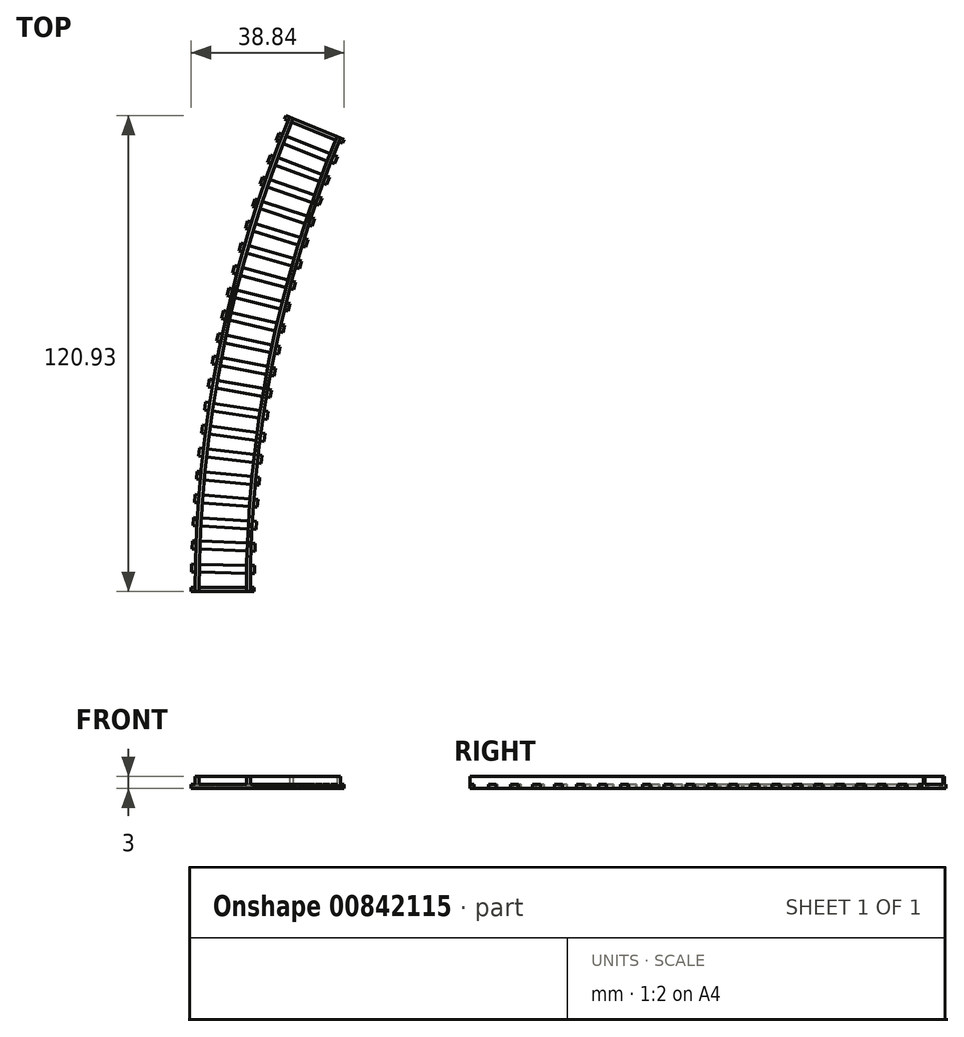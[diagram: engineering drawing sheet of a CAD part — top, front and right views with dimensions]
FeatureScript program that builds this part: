
annotation { "Feature Type Name" : "Feature", "Feature Type Description" : "" }
export const myFeature = defineFeature(function(context is Context, id is Id, definition is map)
    precondition{}
    {
        {
            var Q0;
            Q0=qCreatedBy(makeId("Top.planeOp"),FACE);
            var sketch = newSketch(context, id + "F0", { "sketchPlane" : qUnion([Q0])});
            skCircle(sketch, "E0", {"center": v(0, 0) * mm, "radius": 314 * mm});
            skCircle(sketch, "E1", {"center": v(0, 0) * mm, "radius": 302 * mm});
            skLineSegment(sketch, "E2", {"start": v(0, 0) * mm, "end": v(-293.77, 116.43) * mm});
            skLineSegment(sketch, "E3", {"start": v(0, 0) * mm, "end": v(-369.38, 153) * mm});
            skCircle(sketch, "E4", {"center": v(0, 0) * mm, "radius": 301 * mm});
            skCircle(sketch, "E5", {"center": v(0, 0) * mm, "radius": 315 * mm});
            skLineSegment(sketch, "E6", {"start": v(-293.77, 116.43) * mm, "end": v(-294.5, 114.57) * mm});
            skLineSegment(sketch, "E7", {"start": v(-294.5, 114.57) * mm, "end": v(-279.63, 108.67) * mm});
            skLineSegment(sketch, "E8", {"start": v(-279.63, 108.67) * mm, "end": v(-278.9, 110.53) * mm});
            skLineSegment(sketch, "E9", {"start": v(0, 0) * mm, "end": v(-295.9, 110.91) * mm});
            skLineSegment(sketch, "E10", {"start": v(-295.9, 110.91) * mm, "end": v(-296.6, 109.04) * mm});
            skLineSegment(sketch, "E11", {"start": v(-296.6, 109.04) * mm, "end": v(-281.62, 103.43) * mm});
            skLineSegment(sketch, "E12", {"start": v(-281.62, 103.43) * mm, "end": v(-280.91, 105.3) * mm});
            skLineSegment(sketch, "E13", {"start": v(-280.91, 105.3) * mm, "end": v(-279.63, 108.67) * mm, "construction": true});
            skLineSegment(sketch, "E14", {"start": v(0, 0) * mm, "end": v(-297.92, 105.36) * mm});
            skLineSegment(sketch, "E15", {"start": v(0, 0) * mm, "end": v(-299.84, 99.77) * mm});
            skLineSegment(sketch, "E16", {"start": v(0, 0) * mm, "end": v(-301.65, 94.15) * mm});
            skLineSegment(sketch, "E17", {"start": v(0, 0) * mm, "end": v(-303.36, 88.5) * mm});
            skLineSegment(sketch, "E18", {"start": v(0, 0) * mm, "end": v(-304.96, 82.8) * mm});
            skLineSegment(sketch, "E19", {"start": v(0, 0) * mm, "end": v(-306.45, 77.09) * mm});
            skLineSegment(sketch, "E20", {"start": v(0, 0) * mm, "end": v(-307.84, 71.34) * mm});
            skLineSegment(sketch, "E21", {"start": v(0, 0) * mm, "end": v(-309.12, 65.57) * mm});
            skLineSegment(sketch, "E22", {"start": v(0, 0) * mm, "end": v(-310.3, 59.78) * mm});
            skLineSegment(sketch, "E23", {"start": v(0, 0) * mm, "end": v(-311.36, 53.97) * mm});
            skLineSegment(sketch, "E24", {"start": v(0, 0) * mm, "end": v(-312.31, 48.14) * mm});
            skLineSegment(sketch, "E25", {"start": v(0, 0) * mm, "end": v(-313.16, 42.3) * mm});
            skLineSegment(sketch, "E26", {"start": v(0, 0) * mm, "end": v(-313.9, 36.43) * mm});
            skLineSegment(sketch, "E27", {"start": v(0, 0) * mm, "end": v(-314.52, 30.55) * mm});
            skLineSegment(sketch, "E28", {"start": v(0, 0) * mm, "end": v(-315.04, 24.66) * mm});
            skLineSegment(sketch, "E29", {"start": v(0, 0) * mm, "end": v(-315.44, 18.77) * mm});
            skLineSegment(sketch, "E30", {"start": v(-297.92, 105.36) * mm, "end": v(-298.58, 103.48) * mm});
            skLineSegment(sketch, "E31", {"start": v(-298.58, 103.48) * mm, "end": v(-283.5, 98.14) * mm});
            skLineSegment(sketch, "E32", {"start": v(-283.5, 98.14) * mm, "end": v(-282.83, 100.03) * mm});
            skLineSegment(sketch, "E33", {"start": v(-299.84, 99.77) * mm, "end": v(-300.47, 97.87) * mm});
            skLineSegment(sketch, "E34", {"start": v(-300.47, 97.87) * mm, "end": v(-285.29, 92.82) * mm});
            skLineSegment(sketch, "E35", {"start": v(-285.29, 92.82) * mm, "end": v(-284.65, 94.72) * mm});
            skLineSegment(sketch, "E36", {"start": v(-301.65, 94.15) * mm, "end": v(-302.24, 92.24) * mm});
            skLineSegment(sketch, "E37", {"start": v(-302.24, 92.24) * mm, "end": v(-286.97, 87.47) * mm});
            skLineSegment(sketch, "E38", {"start": v(-286.97, 87.47) * mm, "end": v(-286.38, 89.38) * mm});
            skLineSegment(sketch, "E39", {"start": v(-303.36, 88.5) * mm, "end": v(-303.92, 86.57) * mm});
            skLineSegment(sketch, "E40", {"start": v(-303.92, 86.57) * mm, "end": v(-288.56, 82.1) * mm});
            skLineSegment(sketch, "E41", {"start": v(-288.56, 82.1) * mm, "end": v(-288, 84.01) * mm});
            skLineSegment(sketch, "E42", {"start": v(-304.96, 82.8) * mm, "end": v(-305.48, 80.87) * mm});
            skLineSegment(sketch, "E43", {"start": v(-305.48, 80.87) * mm, "end": v(-290.04, 76.68) * mm});
            skLineSegment(sketch, "E44", {"start": v(-290.04, 76.68) * mm, "end": v(-289.52, 78.61) * mm});
            skLineSegment(sketch, "E45", {"start": v(-306.45, 77.09) * mm, "end": v(-306.94, 75.15) * mm});
            skLineSegment(sketch, "E46", {"start": v(-306.94, 75.15) * mm, "end": v(-291.42, 71.24) * mm});
            skLineSegment(sketch, "E47", {"start": v(-291.42, 71.24) * mm, "end": v(-290.94, 73.18) * mm});
            skLineSegment(sketch, "E48", {"start": v(-307.84, 71.34) * mm, "end": v(-308.3, 69.4) * mm});
            skLineSegment(sketch, "E49", {"start": v(-308.3, 69.4) * mm, "end": v(-292.7, 65.78) * mm});
            skLineSegment(sketch, "E50", {"start": v(-292.7, 65.78) * mm, "end": v(-292.25, 67.73) * mm});
            skLineSegment(sketch, "E51", {"start": v(-309.12, 65.57) * mm, "end": v(-309.54, 63.62) * mm});
            skLineSegment(sketch, "E52", {"start": v(-309.54, 63.62) * mm, "end": v(-293.88, 60.3) * mm});
            skLineSegment(sketch, "E53", {"start": v(-293.88, 60.3) * mm, "end": v(-293.47, 62.25) * mm});
            skLineSegment(sketch, "E54", {"start": v(-310.3, 59.78) * mm, "end": v(-310.67, 57.82) * mm});
            skLineSegment(sketch, "E55", {"start": v(-310.67, 57.82) * mm, "end": v(-294.96, 54.8) * mm});
            skLineSegment(sketch, "E56", {"start": v(-294.96, 54.8) * mm, "end": v(-294.58, 56.76) * mm});
            skLineSegment(sketch, "E57", {"start": v(-311.36, 53.97) * mm, "end": v(-311.7, 52) * mm});
            skLineSegment(sketch, "E58", {"start": v(-311.7, 52) * mm, "end": v(-295.93, 49.27) * mm});
            skLineSegment(sketch, "E59", {"start": v(-295.93, 49.27) * mm, "end": v(-295.6, 51.24) * mm});
            skLineSegment(sketch, "E60", {"start": v(-312.31, 48.14) * mm, "end": v(-312.62, 46.16) * mm});
            skLineSegment(sketch, "E61", {"start": v(-312.62, 46.16) * mm, "end": v(-296.8, 43.72) * mm});
            skLineSegment(sketch, "E62", {"start": v(-296.8, 43.72) * mm, "end": v(-296.5, 45.7) * mm});
            skLineSegment(sketch, "E63", {"start": v(-313.16, 42.3) * mm, "end": v(-313.43, 40.3) * mm});
            skLineSegment(sketch, "E64", {"start": v(-313.43, 40.3) * mm, "end": v(-297.57, 38.17) * mm});
            skLineSegment(sketch, "E65", {"start": v(-297.57, 38.17) * mm, "end": v(-297.3, 40.15) * mm});
            skLineSegment(sketch, "E66", {"start": v(-313.9, 36.43) * mm, "end": v(-314.12, 34.44) * mm});
            skLineSegment(sketch, "E67", {"start": v(-314.12, 34.44) * mm, "end": v(-298.23, 32.6) * mm});
            skLineSegment(sketch, "E68", {"start": v(-298.23, 32.6) * mm, "end": v(-298, 34.58) * mm});
            skLineSegment(sketch, "E69", {"start": v(-314.52, 30.55) * mm, "end": v(-314.71, 28.56) * mm});
            skLineSegment(sketch, "E70", {"start": v(-314.71, 28.56) * mm, "end": v(-298.79, 27.01) * mm});
            skLineSegment(sketch, "E71", {"start": v(-298.79, 27.01) * mm, "end": v(-298.6, 29) * mm});
            skLineSegment(sketch, "E72", {"start": v(-315.04, 24.66) * mm, "end": v(-315.2, 22.67) * mm});
            skLineSegment(sketch, "E73", {"start": v(-315.2, 22.67) * mm, "end": v(-299.24, 21.42) * mm});
            skLineSegment(sketch, "E74", {"start": v(-299.24, 21.42) * mm, "end": v(-299.08, 23.42) * mm});
            skLineSegment(sketch, "E75", {"start": v(-315.44, 18.77) * mm, "end": v(-315.56, 16.77) * mm});
            skLineSegment(sketch, "E76", {"start": v(-315.56, 16.77) * mm, "end": v(-299.59, 15.82) * mm});
            skLineSegment(sketch, "E77", {"start": v(-299.59, 15.82) * mm, "end": v(-299.47, 17.82) * mm});
            skLineSegment(sketch, "E78", {"start": v(-281.62, 103.43) * mm, "end": v(-282.83, 100.03) * mm, "construction": true});
            skLineSegment(sketch, "E79", {"start": v(-283.5, 98.14) * mm, "end": v(-284.65, 94.72) * mm, "construction": true});
            skLineSegment(sketch, "E80", {"start": v(-285.29, 92.82) * mm, "end": v(-286.38, 89.38) * mm, "construction": true});
            skLineSegment(sketch, "E81", {"start": v(-286.97, 87.47) * mm, "end": v(-288, 84.01) * mm, "construction": true});
            skLineSegment(sketch, "E82", {"start": v(-288.56, 82.1) * mm, "end": v(-289.52, 78.61) * mm, "construction": true});
            skLineSegment(sketch, "E83", {"start": v(-290.04, 76.68) * mm, "end": v(-290.94, 73.18) * mm, "construction": true});
            skLineSegment(sketch, "E84", {"start": v(-291.42, 71.24) * mm, "end": v(-292.25, 67.73) * mm, "construction": true});
            skLineSegment(sketch, "E85", {"start": v(-292.7, 65.78) * mm, "end": v(-293.47, 62.25) * mm, "construction": true});
            skLineSegment(sketch, "E86", {"start": v(-293.88, 60.3) * mm, "end": v(-294.58, 56.76) * mm, "construction": true});
            skLineSegment(sketch, "E87", {"start": v(-294.96, 54.8) * mm, "end": v(-295.6, 51.24) * mm, "construction": true});
            skLineSegment(sketch, "E88", {"start": v(-295.93, 49.27) * mm, "end": v(-296.5, 45.7) * mm, "construction": true});
            skLineSegment(sketch, "E89", {"start": v(-296.8, 43.72) * mm, "end": v(-297.3, 40.15) * mm, "construction": true});
            skLineSegment(sketch, "E90", {"start": v(-297.57, 38.17) * mm, "end": v(-298, 34.58) * mm, "construction": true});
            skLineSegment(sketch, "E91", {"start": v(-298.23, 32.6) * mm, "end": v(-298.6, 29) * mm, "construction": true});
            skLineSegment(sketch, "E92", {"start": v(-298.79, 27.01) * mm, "end": v(-299.08, 23.42) * mm, "construction": true});
            skLineSegment(sketch, "E93", {"start": v(-299.24, 21.42) * mm, "end": v(-299.47, 17.82) * mm, "construction": true});
            skLineSegment(sketch, "E94", {"start": v(0, 0) * mm, "end": v(-315.74, 12.87) * mm});
            skLineSegment(sketch, "E95", {"start": v(-315.74, 12.87) * mm, "end": v(-315.82, 10.87) * mm});
            skLineSegment(sketch, "E96", {"start": v(-315.82, 10.87) * mm, "end": v(-299.83, 10.22) * mm});
            skLineSegment(sketch, "E97", {"start": v(-299.83, 10.22) * mm, "end": v(-299.75, 12.22) * mm});
            skLineSegment(sketch, "E98", {"start": v(-299.75, 12.22) * mm, "end": v(-299.59, 15.82) * mm, "construction": true});
            skLineSegment(sketch, "E99.bottom", {"start": v(-469.53, 106.99) * mm, "end": v(-349.53, 106.99) * mm, "construction": true});
            skLineSegment(sketch, "E99.top", {"start": v(-469.53, -13.01) * mm, "end": v(-349.53, -13.01) * mm, "construction": true});
            skLineSegment(sketch, "E99.left", {"start": v(-469.53, 106.99) * mm, "end": v(-469.53, -13.01) * mm, "construction": true});
            skLineSegment(sketch, "E99.right", {"start": v(-349.53, 106.99) * mm, "end": v(-349.53, -13.01) * mm, "construction": true});
            skLineSegment(sketch, "E100", {"start": v(-301, 0) * mm, "end": v(-315, 0) * mm});
            skLineSegment(sketch, "E101", {"start": v(0, 0) * mm, "end": v(-291.95, 120.93) * mm});
            skLineSegment(sketch, "E102", {"start": v(-291.95, 120.93) * mm, "end": v(-292.33, 120) * mm});
            skLineSegment(sketch, "E103", {"start": v(-292.33, 120) * mm, "end": v(-277.55, 113.88) * mm});
            skLineSegment(sketch, "E104", {"start": v(-277.55, 113.88) * mm, "end": v(-277.16, 114.8) * mm});
            skLineSegment(sketch, "E105", {"start": v(-277.16, 114.8) * mm, "end": v(-277.16, 114.8) * mm});
            skLineSegment(sketch, "E106", {"start": v(-278.9, 110.53) * mm, "end": v(-277.55, 113.88) * mm, "construction": true});
            skLineSegment(sketch, "E107", {"start": v(0, 0) * mm, "end": v(-315.92, 6.96) * mm});
            skLineSegment(sketch, "E108", {"start": v(0, 0) * mm, "end": v(-316, 0) * mm});
            skLineSegment(sketch, "E109", {"start": v(-316, 1) * mm, "end": v(-316, 0) * mm});
            skLineSegment(sketch, "E110", {"start": v(-316, 1) * mm, "end": v(-300, 1) * mm});
            skLineSegment(sketch, "E111", {"start": v(-300, 0) * mm, "end": v(-300, 1) * mm});
            skLineSegment(sketch, "E112", {"start": v(-315.92, 6.96) * mm, "end": v(-315.97, 4.96) * mm});
            skLineSegment(sketch, "E113", {"start": v(-315.97, 4.96) * mm, "end": v(-299.97, 4.6) * mm});
            skLineSegment(sketch, "E114", {"start": v(-299.97, 4.6) * mm, "end": v(-299.97, 6.61) * mm});
            skLineSegment(sketch, "E115", {"start": v(-299.97, 6.61) * mm, "end": v(-299.83, 10.22) * mm, "construction": true});
            skLineSegment(sketch, "E116", {"start": v(-299.97, 4.6) * mm, "end": v(-300, 1) * mm, "construction": true});
            skSolve(sketch);
        }
        {
            var Q0;
            {var subQ0=sQuery(id+"F0.wireOp",EDGE,"E103");var subQ1=sQuery(id+"F0.wireOp",EDGE,"E0");var subQ2=makeQuery(id+"F0.imprint","INTERSECT",VERTEX,{"derivedFrom":[subQ1,subQ0]});Q0=makeQuery(id+"F0.imprint","IMPRINT",FACE,{"disambiguationData":[TD([[makeQuery(id+"F0.imprint","IMPRINT",EDGE,{"disambiguationData":[TD([[subQ2,-1.0]])],"derivedFrom":subQ1}),-1.0]])]});}
            var Q1;
            {var subQ0=sQuery(id+"F0.wireOp",EDGE,"E7");var subQ1=sQuery(id+"F0.wireOp",EDGE,"E0");var subQ2=makeQuery(id+"F0.imprint","INTERSECT",VERTEX,{"derivedFrom":[subQ1,subQ0]});Q1=makeQuery(id+"F0.imprint","IMPRINT",FACE,{"disambiguationData":[TD([[makeQuery(id+"F0.imprint","IMPRINT",EDGE,{"disambiguationData":[TD([[subQ2,-1.0]])],"derivedFrom":subQ1}),-1.0]])]});}
            var Q2;
            {var subQ0=sQuery(id+"F0.wireOp",EDGE,"E11");var subQ1=sQuery(id+"F0.wireOp",EDGE,"E0");var subQ2=makeQuery(id+"F0.imprint","INTERSECT",VERTEX,{"derivedFrom":[subQ1,subQ0]});Q2=makeQuery(id+"F0.imprint","IMPRINT",FACE,{"disambiguationData":[TD([[makeQuery(id+"F0.imprint","IMPRINT",EDGE,{"disambiguationData":[TD([[subQ2,-1.0]])],"derivedFrom":subQ1}),-1.0]])]});}
            var Q3;
            {var subQ0=sQuery(id+"F0.wireOp",EDGE,"E31");var subQ1=sQuery(id+"F0.wireOp",EDGE,"E0");var subQ2=makeQuery(id+"F0.imprint","INTERSECT",VERTEX,{"derivedFrom":[subQ1,subQ0]});Q3=makeQuery(id+"F0.imprint","IMPRINT",FACE,{"disambiguationData":[TD([[makeQuery(id+"F0.imprint","IMPRINT",EDGE,{"disambiguationData":[TD([[subQ2,-1.0]])],"derivedFrom":subQ1}),-1.0]])]});}
            var Q4;
            {var subQ0=sQuery(id+"F0.wireOp",EDGE,"E34");var subQ1=sQuery(id+"F0.wireOp",EDGE,"E0");var subQ2=makeQuery(id+"F0.imprint","INTERSECT",VERTEX,{"derivedFrom":[subQ1,subQ0]});Q4=makeQuery(id+"F0.imprint","IMPRINT",FACE,{"disambiguationData":[TD([[makeQuery(id+"F0.imprint","IMPRINT",EDGE,{"disambiguationData":[TD([[subQ2,-1.0]])],"derivedFrom":subQ1}),-1.0]])]});}
            var Q5;
            {var subQ0=sQuery(id+"F0.wireOp",EDGE,"E37");var subQ1=sQuery(id+"F0.wireOp",EDGE,"E0");var subQ2=makeQuery(id+"F0.imprint","INTERSECT",VERTEX,{"derivedFrom":[subQ1,subQ0]});Q5=makeQuery(id+"F0.imprint","IMPRINT",FACE,{"disambiguationData":[TD([[makeQuery(id+"F0.imprint","IMPRINT",EDGE,{"disambiguationData":[TD([[subQ2,-1.0]])],"derivedFrom":subQ1}),-1.0]])]});}
            var Q6;
            {var subQ0=sQuery(id+"F0.wireOp",EDGE,"E40");var subQ1=sQuery(id+"F0.wireOp",EDGE,"E0");var subQ2=makeQuery(id+"F0.imprint","INTERSECT",VERTEX,{"derivedFrom":[subQ1,subQ0]});Q6=makeQuery(id+"F0.imprint","IMPRINT",FACE,{"disambiguationData":[TD([[makeQuery(id+"F0.imprint","IMPRINT",EDGE,{"disambiguationData":[TD([[subQ2,-1.0]])],"derivedFrom":subQ1}),-1.0]])]});}
            var Q7;
            {var subQ0=sQuery(id+"F0.wireOp",EDGE,"E43");var subQ1=sQuery(id+"F0.wireOp",EDGE,"E0");var subQ2=makeQuery(id+"F0.imprint","INTERSECT",VERTEX,{"derivedFrom":[subQ1,subQ0]});Q7=makeQuery(id+"F0.imprint","IMPRINT",FACE,{"disambiguationData":[TD([[makeQuery(id+"F0.imprint","IMPRINT",EDGE,{"disambiguationData":[TD([[subQ2,-1.0]])],"derivedFrom":subQ1}),-1.0]])]});}
            var Q8;
            {var subQ0=sQuery(id+"F0.wireOp",EDGE,"E46");var subQ1=sQuery(id+"F0.wireOp",EDGE,"E0");var subQ2=makeQuery(id+"F0.imprint","INTERSECT",VERTEX,{"derivedFrom":[subQ1,subQ0]});Q8=makeQuery(id+"F0.imprint","IMPRINT",FACE,{"disambiguationData":[TD([[makeQuery(id+"F0.imprint","IMPRINT",EDGE,{"disambiguationData":[TD([[subQ2,-1.0]])],"derivedFrom":subQ1}),-1.0]])]});}
            var Q9;
            {var subQ0=sQuery(id+"F0.wireOp",EDGE,"E49");var subQ1=sQuery(id+"F0.wireOp",EDGE,"E0");var subQ2=makeQuery(id+"F0.imprint","INTERSECT",VERTEX,{"derivedFrom":[subQ1,subQ0]});Q9=makeQuery(id+"F0.imprint","IMPRINT",FACE,{"disambiguationData":[TD([[makeQuery(id+"F0.imprint","IMPRINT",EDGE,{"disambiguationData":[TD([[subQ2,-1.0]])],"derivedFrom":subQ1}),-1.0]])]});}
            var Q10;
            {var subQ0=sQuery(id+"F0.wireOp",EDGE,"E52");var subQ1=sQuery(id+"F0.wireOp",EDGE,"E0");var subQ2=makeQuery(id+"F0.imprint","INTERSECT",VERTEX,{"derivedFrom":[subQ1,subQ0]});Q10=makeQuery(id+"F0.imprint","IMPRINT",FACE,{"disambiguationData":[TD([[makeQuery(id+"F0.imprint","IMPRINT",EDGE,{"disambiguationData":[TD([[subQ2,-1.0]])],"derivedFrom":subQ1}),-1.0]])]});}
            var Q11;
            {var subQ0=sQuery(id+"F0.wireOp",EDGE,"E55");var subQ1=sQuery(id+"F0.wireOp",EDGE,"E0");var subQ2=makeQuery(id+"F0.imprint","INTERSECT",VERTEX,{"derivedFrom":[subQ1,subQ0]});Q11=makeQuery(id+"F0.imprint","IMPRINT",FACE,{"disambiguationData":[TD([[makeQuery(id+"F0.imprint","IMPRINT",EDGE,{"disambiguationData":[TD([[subQ2,-1.0]])],"derivedFrom":subQ1}),-1.0]])]});}
            var Q12;
            {var subQ0=sQuery(id+"F0.wireOp",EDGE,"E58");var subQ1=sQuery(id+"F0.wireOp",EDGE,"E0");var subQ2=makeQuery(id+"F0.imprint","INTERSECT",VERTEX,{"derivedFrom":[subQ1,subQ0]});Q12=makeQuery(id+"F0.imprint","IMPRINT",FACE,{"disambiguationData":[TD([[makeQuery(id+"F0.imprint","IMPRINT",EDGE,{"disambiguationData":[TD([[subQ2,-1.0]])],"derivedFrom":subQ1}),-1.0]])]});}
            var Q13;
            {var subQ0=sQuery(id+"F0.wireOp",EDGE,"E61");var subQ1=sQuery(id+"F0.wireOp",EDGE,"E0");var subQ2=makeQuery(id+"F0.imprint","INTERSECT",VERTEX,{"derivedFrom":[subQ1,subQ0]});Q13=makeQuery(id+"F0.imprint","IMPRINT",FACE,{"disambiguationData":[TD([[makeQuery(id+"F0.imprint","IMPRINT",EDGE,{"disambiguationData":[TD([[subQ2,-1.0]])],"derivedFrom":subQ1}),-1.0]])]});}
            var Q14;
            {var subQ0=sQuery(id+"F0.wireOp",EDGE,"E64");var subQ1=sQuery(id+"F0.wireOp",EDGE,"E0");var subQ2=makeQuery(id+"F0.imprint","INTERSECT",VERTEX,{"derivedFrom":[subQ1,subQ0]});Q14=makeQuery(id+"F0.imprint","IMPRINT",FACE,{"disambiguationData":[TD([[makeQuery(id+"F0.imprint","IMPRINT",EDGE,{"disambiguationData":[TD([[subQ2,-1.0]])],"derivedFrom":subQ1}),-1.0]])]});}
            var Q15;
            {var subQ0=sQuery(id+"F0.wireOp",EDGE,"E67");var subQ1=sQuery(id+"F0.wireOp",EDGE,"E0");var subQ2=makeQuery(id+"F0.imprint","INTERSECT",VERTEX,{"derivedFrom":[subQ1,subQ0]});Q15=makeQuery(id+"F0.imprint","IMPRINT",FACE,{"disambiguationData":[TD([[makeQuery(id+"F0.imprint","IMPRINT",EDGE,{"disambiguationData":[TD([[subQ2,-1.0]])],"derivedFrom":subQ1}),-1.0]])]});}
            var Q16;
            {var subQ0=sQuery(id+"F0.wireOp",EDGE,"E70");var subQ1=sQuery(id+"F0.wireOp",EDGE,"E0");var subQ2=makeQuery(id+"F0.imprint","INTERSECT",VERTEX,{"derivedFrom":[subQ1,subQ0]});Q16=makeQuery(id+"F0.imprint","IMPRINT",FACE,{"disambiguationData":[TD([[makeQuery(id+"F0.imprint","IMPRINT",EDGE,{"disambiguationData":[TD([[subQ2,-1.0]])],"derivedFrom":subQ1}),-1.0]])]});}
            var Q17;
            {var subQ0=sQuery(id+"F0.wireOp",EDGE,"E73");var subQ1=sQuery(id+"F0.wireOp",EDGE,"E0");var subQ2=makeQuery(id+"F0.imprint","INTERSECT",VERTEX,{"derivedFrom":[subQ1,subQ0]});Q17=makeQuery(id+"F0.imprint","IMPRINT",FACE,{"disambiguationData":[TD([[makeQuery(id+"F0.imprint","IMPRINT",EDGE,{"disambiguationData":[TD([[subQ2,-1.0]])],"derivedFrom":subQ1}),-1.0]])]});}
            var Q18;
            {var subQ0=sQuery(id+"F0.wireOp",EDGE,"E76");var subQ1=sQuery(id+"F0.wireOp",EDGE,"E0");var subQ2=makeQuery(id+"F0.imprint","INTERSECT",VERTEX,{"derivedFrom":[subQ1,subQ0]});Q18=makeQuery(id+"F0.imprint","IMPRINT",FACE,{"disambiguationData":[TD([[makeQuery(id+"F0.imprint","IMPRINT",EDGE,{"disambiguationData":[TD([[subQ2,-1.0]])],"derivedFrom":subQ1}),-1.0]])]});}
            var Q19;
            {var subQ0=sQuery(id+"F0.wireOp",EDGE,"E96");var subQ1=sQuery(id+"F0.wireOp",EDGE,"E0");var subQ2=makeQuery(id+"F0.imprint","INTERSECT",VERTEX,{"derivedFrom":[subQ1,subQ0]});Q19=makeQuery(id+"F0.imprint","IMPRINT",FACE,{"disambiguationData":[TD([[makeQuery(id+"F0.imprint","IMPRINT",EDGE,{"disambiguationData":[TD([[subQ2,-1.0]])],"derivedFrom":subQ1}),-1.0]])]});}
            var Q20;
            {var subQ0=sQuery(id+"F0.wireOp",EDGE,"E113");var subQ1=sQuery(id+"F0.wireOp",EDGE,"E0");var subQ2=makeQuery(id+"F0.imprint","INTERSECT",VERTEX,{"derivedFrom":[subQ1,subQ0]});Q20=makeQuery(id+"F0.imprint","IMPRINT",FACE,{"disambiguationData":[TD([[makeQuery(id+"F0.imprint","IMPRINT",EDGE,{"disambiguationData":[TD([[subQ2,-1.0]])],"derivedFrom":subQ1}),-1.0]])]});}
            var Q21;
            {var subQ0=sQuery(id+"F0.wireOp",EDGE,"E103");var subQ1=sQuery(id+"F0.wireOp",EDGE,"E0");var subQ2=makeQuery(id+"F0.imprint","INTERSECT",VERTEX,{"derivedFrom":[subQ1,subQ0]});Q21=makeQuery(id+"F0.imprint","IMPRINT",FACE,{"disambiguationData":[TD([[makeQuery(id+"F0.imprint","IMPRINT",EDGE,{"disambiguationData":[TD([[subQ2,1.0]])],"derivedFrom":subQ1}),-1.0]])]});}
            var Q22;
            {var subQ0=sQuery(id+"F0.wireOp",EDGE,"E2");var subQ1=sQuery(id+"F0.wireOp",EDGE,"E0");var subQ2=makeQuery(id+"F0.imprint","INTERSECT",VERTEX,{"derivedFrom":[subQ1,subQ0]});Q22=makeQuery(id+"F0.imprint","IMPRINT",FACE,{"disambiguationData":[TD([[makeQuery(id+"F0.imprint","IMPRINT",EDGE,{"disambiguationData":[TD([[subQ2,-1.0]])],"derivedFrom":subQ1}),-1.0]])]});}
            var Q23;
            {var subQ0=sQuery(id+"F0.wireOp",EDGE,"E9");var subQ1=sQuery(id+"F0.wireOp",EDGE,"E0");var subQ2=makeQuery(id+"F0.imprint","INTERSECT",VERTEX,{"derivedFrom":[subQ1,subQ0]});Q23=makeQuery(id+"F0.imprint","IMPRINT",FACE,{"disambiguationData":[TD([[makeQuery(id+"F0.imprint","IMPRINT",EDGE,{"disambiguationData":[TD([[subQ2,-1.0]])],"derivedFrom":subQ1}),-1.0]])]});}
            var Q24;
            {var subQ0=sQuery(id+"F0.wireOp",EDGE,"E14");var subQ1=sQuery(id+"F0.wireOp",EDGE,"E0");var subQ2=makeQuery(id+"F0.imprint","INTERSECT",VERTEX,{"derivedFrom":[subQ1,subQ0]});Q24=makeQuery(id+"F0.imprint","IMPRINT",FACE,{"disambiguationData":[TD([[makeQuery(id+"F0.imprint","IMPRINT",EDGE,{"disambiguationData":[TD([[subQ2,-1.0]])],"derivedFrom":subQ1}),-1.0]])]});}
            var Q25;
            {var subQ0=sQuery(id+"F0.wireOp",EDGE,"E15");var subQ1=sQuery(id+"F0.wireOp",EDGE,"E0");var subQ2=makeQuery(id+"F0.imprint","INTERSECT",VERTEX,{"derivedFrom":[subQ1,subQ0]});Q25=makeQuery(id+"F0.imprint","IMPRINT",FACE,{"disambiguationData":[TD([[makeQuery(id+"F0.imprint","IMPRINT",EDGE,{"disambiguationData":[TD([[subQ2,-1.0]])],"derivedFrom":subQ1}),-1.0]])]});}
            var Q26;
            {var subQ0=sQuery(id+"F0.wireOp",EDGE,"E16");var subQ1=sQuery(id+"F0.wireOp",EDGE,"E0");var subQ2=makeQuery(id+"F0.imprint","INTERSECT",VERTEX,{"derivedFrom":[subQ1,subQ0]});Q26=makeQuery(id+"F0.imprint","IMPRINT",FACE,{"disambiguationData":[TD([[makeQuery(id+"F0.imprint","IMPRINT",EDGE,{"disambiguationData":[TD([[subQ2,-1.0]])],"derivedFrom":subQ1}),-1.0]])]});}
            var Q27;
            {var subQ0=sQuery(id+"F0.wireOp",EDGE,"E17");var subQ1=sQuery(id+"F0.wireOp",EDGE,"E0");var subQ2=makeQuery(id+"F0.imprint","INTERSECT",VERTEX,{"derivedFrom":[subQ1,subQ0]});Q27=makeQuery(id+"F0.imprint","IMPRINT",FACE,{"disambiguationData":[TD([[makeQuery(id+"F0.imprint","IMPRINT",EDGE,{"disambiguationData":[TD([[subQ2,-1.0]])],"derivedFrom":subQ1}),-1.0]])]});}
            var Q28;
            {var subQ0=sQuery(id+"F0.wireOp",EDGE,"E18");var subQ1=sQuery(id+"F0.wireOp",EDGE,"E0");var subQ2=makeQuery(id+"F0.imprint","INTERSECT",VERTEX,{"derivedFrom":[subQ1,subQ0]});Q28=makeQuery(id+"F0.imprint","IMPRINT",FACE,{"disambiguationData":[TD([[makeQuery(id+"F0.imprint","IMPRINT",EDGE,{"disambiguationData":[TD([[subQ2,-1.0]])],"derivedFrom":subQ1}),-1.0]])]});}
            var Q29;
            {var subQ0=sQuery(id+"F0.wireOp",EDGE,"E19");var subQ1=sQuery(id+"F0.wireOp",EDGE,"E0");var subQ2=makeQuery(id+"F0.imprint","INTERSECT",VERTEX,{"derivedFrom":[subQ1,subQ0]});Q29=makeQuery(id+"F0.imprint","IMPRINT",FACE,{"disambiguationData":[TD([[makeQuery(id+"F0.imprint","IMPRINT",EDGE,{"disambiguationData":[TD([[subQ2,-1.0]])],"derivedFrom":subQ1}),-1.0]])]});}
            var Q30;
            {var subQ0=sQuery(id+"F0.wireOp",EDGE,"E20");var subQ1=sQuery(id+"F0.wireOp",EDGE,"E0");var subQ2=makeQuery(id+"F0.imprint","INTERSECT",VERTEX,{"derivedFrom":[subQ1,subQ0]});Q30=makeQuery(id+"F0.imprint","IMPRINT",FACE,{"disambiguationData":[TD([[makeQuery(id+"F0.imprint","IMPRINT",EDGE,{"disambiguationData":[TD([[subQ2,-1.0]])],"derivedFrom":subQ1}),-1.0]])]});}
            var Q31;
            {var subQ0=sQuery(id+"F0.wireOp",EDGE,"E21");var subQ1=sQuery(id+"F0.wireOp",EDGE,"E0");var subQ2=makeQuery(id+"F0.imprint","INTERSECT",VERTEX,{"derivedFrom":[subQ1,subQ0]});Q31=makeQuery(id+"F0.imprint","IMPRINT",FACE,{"disambiguationData":[TD([[makeQuery(id+"F0.imprint","IMPRINT",EDGE,{"disambiguationData":[TD([[subQ2,-1.0]])],"derivedFrom":subQ1}),-1.0]])]});}
            var Q32;
            {var subQ0=sQuery(id+"F0.wireOp",EDGE,"E22");var subQ1=sQuery(id+"F0.wireOp",EDGE,"E0");var subQ2=makeQuery(id+"F0.imprint","INTERSECT",VERTEX,{"derivedFrom":[subQ1,subQ0]});Q32=makeQuery(id+"F0.imprint","IMPRINT",FACE,{"disambiguationData":[TD([[makeQuery(id+"F0.imprint","IMPRINT",EDGE,{"disambiguationData":[TD([[subQ2,-1.0]])],"derivedFrom":subQ1}),-1.0]])]});}
            var Q33;
            {var subQ0=sQuery(id+"F0.wireOp",EDGE,"E23");var subQ1=sQuery(id+"F0.wireOp",EDGE,"E0");var subQ2=makeQuery(id+"F0.imprint","INTERSECT",VERTEX,{"derivedFrom":[subQ1,subQ0]});Q33=makeQuery(id+"F0.imprint","IMPRINT",FACE,{"disambiguationData":[TD([[makeQuery(id+"F0.imprint","IMPRINT",EDGE,{"disambiguationData":[TD([[subQ2,-1.0]])],"derivedFrom":subQ1}),-1.0]])]});}
            var Q34;
            {var subQ0=sQuery(id+"F0.wireOp",EDGE,"E24");var subQ1=sQuery(id+"F0.wireOp",EDGE,"E0");var subQ2=makeQuery(id+"F0.imprint","INTERSECT",VERTEX,{"derivedFrom":[subQ1,subQ0]});Q34=makeQuery(id+"F0.imprint","IMPRINT",FACE,{"disambiguationData":[TD([[makeQuery(id+"F0.imprint","IMPRINT",EDGE,{"disambiguationData":[TD([[subQ2,-1.0]])],"derivedFrom":subQ1}),-1.0]])]});}
            var Q35;
            {var subQ0=sQuery(id+"F0.wireOp",EDGE,"E25");var subQ1=sQuery(id+"F0.wireOp",EDGE,"E0");var subQ2=makeQuery(id+"F0.imprint","INTERSECT",VERTEX,{"derivedFrom":[subQ1,subQ0]});Q35=makeQuery(id+"F0.imprint","IMPRINT",FACE,{"disambiguationData":[TD([[makeQuery(id+"F0.imprint","IMPRINT",EDGE,{"disambiguationData":[TD([[subQ2,-1.0]])],"derivedFrom":subQ1}),-1.0]])]});}
            var Q36;
            {var subQ0=sQuery(id+"F0.wireOp",EDGE,"E26");var subQ1=sQuery(id+"F0.wireOp",EDGE,"E0");var subQ2=makeQuery(id+"F0.imprint","INTERSECT",VERTEX,{"derivedFrom":[subQ1,subQ0]});Q36=makeQuery(id+"F0.imprint","IMPRINT",FACE,{"disambiguationData":[TD([[makeQuery(id+"F0.imprint","IMPRINT",EDGE,{"disambiguationData":[TD([[subQ2,-1.0]])],"derivedFrom":subQ1}),-1.0]])]});}
            var Q37;
            {var subQ0=sQuery(id+"F0.wireOp",EDGE,"E27");var subQ1=sQuery(id+"F0.wireOp",EDGE,"E0");var subQ2=makeQuery(id+"F0.imprint","INTERSECT",VERTEX,{"derivedFrom":[subQ1,subQ0]});Q37=makeQuery(id+"F0.imprint","IMPRINT",FACE,{"disambiguationData":[TD([[makeQuery(id+"F0.imprint","IMPRINT",EDGE,{"disambiguationData":[TD([[subQ2,-1.0]])],"derivedFrom":subQ1}),-1.0]])]});}
            var Q38;
            {var subQ0=sQuery(id+"F0.wireOp",EDGE,"E28");var subQ1=sQuery(id+"F0.wireOp",EDGE,"E0");var subQ2=makeQuery(id+"F0.imprint","INTERSECT",VERTEX,{"derivedFrom":[subQ1,subQ0]});Q38=makeQuery(id+"F0.imprint","IMPRINT",FACE,{"disambiguationData":[TD([[makeQuery(id+"F0.imprint","IMPRINT",EDGE,{"disambiguationData":[TD([[subQ2,-1.0]])],"derivedFrom":subQ1}),-1.0]])]});}
            var Q39;
            {var subQ0=sQuery(id+"F0.wireOp",EDGE,"E29");var subQ1=sQuery(id+"F0.wireOp",EDGE,"E0");var subQ2=makeQuery(id+"F0.imprint","INTERSECT",VERTEX,{"derivedFrom":[subQ1,subQ0]});Q39=makeQuery(id+"F0.imprint","IMPRINT",FACE,{"disambiguationData":[TD([[makeQuery(id+"F0.imprint","IMPRINT",EDGE,{"disambiguationData":[TD([[subQ2,-1.0]])],"derivedFrom":subQ1}),-1.0]])]});}
            var Q40;
            {var subQ0=sQuery(id+"F0.wireOp",EDGE,"E94");var subQ1=sQuery(id+"F0.wireOp",EDGE,"E0");var subQ2=makeQuery(id+"F0.imprint","INTERSECT",VERTEX,{"derivedFrom":[subQ1,subQ0]});Q40=makeQuery(id+"F0.imprint","IMPRINT",FACE,{"disambiguationData":[TD([[makeQuery(id+"F0.imprint","IMPRINT",EDGE,{"disambiguationData":[TD([[subQ2,-1.0]])],"derivedFrom":subQ1}),-1.0]])]});}
            var Q41;
            {var subQ0=sQuery(id+"F0.wireOp",EDGE,"E107");var subQ1=sQuery(id+"F0.wireOp",EDGE,"E0");var subQ2=makeQuery(id+"F0.imprint","INTERSECT",VERTEX,{"derivedFrom":[subQ1,subQ0]});Q41=makeQuery(id+"F0.imprint","IMPRINT",FACE,{"disambiguationData":[TD([[makeQuery(id+"F0.imprint","IMPRINT",EDGE,{"disambiguationData":[TD([[subQ2,-1.0]])],"derivedFrom":subQ1}),-1.0]])]});}
            var Q42;
            {var subQ0=sQuery(id+"F0.wireOp",EDGE,"E110");var subQ1=sQuery(id+"F0.wireOp",EDGE,"E0");var subQ2=makeQuery(id+"F0.imprint","INTERSECT",VERTEX,{"derivedFrom":[subQ1,subQ0]});Q42=makeQuery(id+"F0.imprint","IMPRINT",FACE,{"disambiguationData":[TD([[makeQuery(id+"F0.imprint","IMPRINT",EDGE,{"disambiguationData":[TD([[subQ2,-1.0]])],"derivedFrom":subQ1}),-1.0]])]});}
            var Q43;
            {var subQ0=sQuery(id+"F0.wireOp",EDGE,"E67");var subQ1=sQuery(id+"F0.wireOp",EDGE,"E1");var subQ2=makeQuery(id+"F0.imprint","INTERSECT",VERTEX,{"derivedFrom":[subQ1,subQ0]});Q43=makeQuery(id+"F0.imprint","IMPRINT",FACE,{"disambiguationData":[TD([[makeQuery(id+"F0.imprint","IMPRINT",EDGE,{"disambiguationData":[TD([[subQ2,-1.0]])],"derivedFrom":subQ1}),1.0]])]});}
            var Q44;
            {var subQ0=sQuery(id+"F0.wireOp",EDGE,"E27");var subQ1=sQuery(id+"F0.wireOp",EDGE,"E1");var subQ2=makeQuery(id+"F0.imprint","INTERSECT",VERTEX,{"derivedFrom":[subQ1,subQ0]});Q44=makeQuery(id+"F0.imprint","IMPRINT",FACE,{"disambiguationData":[TD([[makeQuery(id+"F0.imprint","IMPRINT",EDGE,{"disambiguationData":[TD([[subQ2,-1.0]])],"derivedFrom":subQ1}),1.0]])]});}
            var Q45;
            {var subQ0=sQuery(id+"F0.wireOp",EDGE,"E70");var subQ1=sQuery(id+"F0.wireOp",EDGE,"E1");var subQ2=makeQuery(id+"F0.imprint","INTERSECT",VERTEX,{"derivedFrom":[subQ1,subQ0]});Q45=makeQuery(id+"F0.imprint","IMPRINT",FACE,{"disambiguationData":[TD([[makeQuery(id+"F0.imprint","IMPRINT",EDGE,{"disambiguationData":[TD([[subQ2,-1.0]])],"derivedFrom":subQ1}),1.0]])]});}
            var Q46;
            {var subQ0=sQuery(id+"F0.wireOp",EDGE,"E28");var subQ1=sQuery(id+"F0.wireOp",EDGE,"E1");var subQ2=makeQuery(id+"F0.imprint","INTERSECT",VERTEX,{"derivedFrom":[subQ1,subQ0]});Q46=makeQuery(id+"F0.imprint","IMPRINT",FACE,{"disambiguationData":[TD([[makeQuery(id+"F0.imprint","IMPRINT",EDGE,{"disambiguationData":[TD([[subQ2,-1.0]])],"derivedFrom":subQ1}),1.0]])]});}
            var Q47;
            {var subQ0=sQuery(id+"F0.wireOp",EDGE,"E73");var subQ1=sQuery(id+"F0.wireOp",EDGE,"E1");var subQ2=makeQuery(id+"F0.imprint","INTERSECT",VERTEX,{"derivedFrom":[subQ1,subQ0]});Q47=makeQuery(id+"F0.imprint","IMPRINT",FACE,{"disambiguationData":[TD([[makeQuery(id+"F0.imprint","IMPRINT",EDGE,{"disambiguationData":[TD([[subQ2,-1.0]])],"derivedFrom":subQ1}),1.0]])]});}
            var Q48;
            {var subQ0=sQuery(id+"F0.wireOp",EDGE,"E29");var subQ1=sQuery(id+"F0.wireOp",EDGE,"E1");var subQ2=makeQuery(id+"F0.imprint","INTERSECT",VERTEX,{"derivedFrom":[subQ1,subQ0]});Q48=makeQuery(id+"F0.imprint","IMPRINT",FACE,{"disambiguationData":[TD([[makeQuery(id+"F0.imprint","IMPRINT",EDGE,{"disambiguationData":[TD([[subQ2,-1.0]])],"derivedFrom":subQ1}),1.0]])]});}
            var Q49;
            {var subQ0=sQuery(id+"F0.wireOp",EDGE,"E76");var subQ1=sQuery(id+"F0.wireOp",EDGE,"E1");var subQ2=makeQuery(id+"F0.imprint","INTERSECT",VERTEX,{"derivedFrom":[subQ1,subQ0]});Q49=makeQuery(id+"F0.imprint","IMPRINT",FACE,{"disambiguationData":[TD([[makeQuery(id+"F0.imprint","IMPRINT",EDGE,{"disambiguationData":[TD([[subQ2,-1.0]])],"derivedFrom":subQ1}),1.0]])]});}
            var Q50;
            {var subQ0=sQuery(id+"F0.wireOp",EDGE,"E94");var subQ1=sQuery(id+"F0.wireOp",EDGE,"E1");var subQ2=makeQuery(id+"F0.imprint","INTERSECT",VERTEX,{"derivedFrom":[subQ1,subQ0]});Q50=makeQuery(id+"F0.imprint","IMPRINT",FACE,{"disambiguationData":[TD([[makeQuery(id+"F0.imprint","IMPRINT",EDGE,{"disambiguationData":[TD([[subQ2,-1.0]])],"derivedFrom":subQ1}),1.0]])]});}
            var Q51;
            {var subQ0=sQuery(id+"F0.wireOp",EDGE,"E96");var subQ1=sQuery(id+"F0.wireOp",EDGE,"E1");var subQ2=makeQuery(id+"F0.imprint","INTERSECT",VERTEX,{"derivedFrom":[subQ1,subQ0]});Q51=makeQuery(id+"F0.imprint","IMPRINT",FACE,{"disambiguationData":[TD([[makeQuery(id+"F0.imprint","IMPRINT",EDGE,{"disambiguationData":[TD([[subQ2,-1.0]])],"derivedFrom":subQ1}),1.0]])]});}
            var Q52;
            {var subQ0=sQuery(id+"F0.wireOp",EDGE,"E26");var subQ1=sQuery(id+"F0.wireOp",EDGE,"E1");var subQ2=makeQuery(id+"F0.imprint","INTERSECT",VERTEX,{"derivedFrom":[subQ1,subQ0]});Q52=makeQuery(id+"F0.imprint","IMPRINT",FACE,{"disambiguationData":[TD([[makeQuery(id+"F0.imprint","IMPRINT",EDGE,{"disambiguationData":[TD([[subQ2,-1.0]])],"derivedFrom":subQ1}),1.0]])]});}
            var Q53;
            {var subQ0=sQuery(id+"F0.wireOp",EDGE,"E64");var subQ1=sQuery(id+"F0.wireOp",EDGE,"E1");var subQ2=makeQuery(id+"F0.imprint","INTERSECT",VERTEX,{"derivedFrom":[subQ1,subQ0]});Q53=makeQuery(id+"F0.imprint","IMPRINT",FACE,{"disambiguationData":[TD([[makeQuery(id+"F0.imprint","IMPRINT",EDGE,{"disambiguationData":[TD([[subQ2,-1.0]])],"derivedFrom":subQ1}),1.0]])]});}
            var Q54;
            {var subQ0=sQuery(id+"F0.wireOp",EDGE,"E25");var subQ1=sQuery(id+"F0.wireOp",EDGE,"E1");var subQ2=makeQuery(id+"F0.imprint","INTERSECT",VERTEX,{"derivedFrom":[subQ1,subQ0]});Q54=makeQuery(id+"F0.imprint","IMPRINT",FACE,{"disambiguationData":[TD([[makeQuery(id+"F0.imprint","IMPRINT",EDGE,{"disambiguationData":[TD([[subQ2,-1.0]])],"derivedFrom":subQ1}),1.0]])]});}
            var Q55;
            {var subQ0=sQuery(id+"F0.wireOp",EDGE,"E61");var subQ1=sQuery(id+"F0.wireOp",EDGE,"E1");var subQ2=makeQuery(id+"F0.imprint","INTERSECT",VERTEX,{"derivedFrom":[subQ1,subQ0]});Q55=makeQuery(id+"F0.imprint","IMPRINT",FACE,{"disambiguationData":[TD([[makeQuery(id+"F0.imprint","IMPRINT",EDGE,{"disambiguationData":[TD([[subQ2,-1.0]])],"derivedFrom":subQ1}),1.0]])]});}
            var Q56;
            {var subQ0=sQuery(id+"F0.wireOp",EDGE,"E24");var subQ1=sQuery(id+"F0.wireOp",EDGE,"E1");var subQ2=makeQuery(id+"F0.imprint","INTERSECT",VERTEX,{"derivedFrom":[subQ1,subQ0]});Q56=makeQuery(id+"F0.imprint","IMPRINT",FACE,{"disambiguationData":[TD([[makeQuery(id+"F0.imprint","IMPRINT",EDGE,{"disambiguationData":[TD([[subQ2,-1.0]])],"derivedFrom":subQ1}),1.0]])]});}
            var Q57;
            {var subQ0=sQuery(id+"F0.wireOp",EDGE,"E58");var subQ1=sQuery(id+"F0.wireOp",EDGE,"E1");var subQ2=makeQuery(id+"F0.imprint","INTERSECT",VERTEX,{"derivedFrom":[subQ1,subQ0]});Q57=makeQuery(id+"F0.imprint","IMPRINT",FACE,{"disambiguationData":[TD([[makeQuery(id+"F0.imprint","IMPRINT",EDGE,{"disambiguationData":[TD([[subQ2,-1.0]])],"derivedFrom":subQ1}),1.0]])]});}
            var Q58;
            {var subQ0=sQuery(id+"F0.wireOp",EDGE,"E23");var subQ1=sQuery(id+"F0.wireOp",EDGE,"E1");var subQ2=makeQuery(id+"F0.imprint","INTERSECT",VERTEX,{"derivedFrom":[subQ1,subQ0]});Q58=makeQuery(id+"F0.imprint","IMPRINT",FACE,{"disambiguationData":[TD([[makeQuery(id+"F0.imprint","IMPRINT",EDGE,{"disambiguationData":[TD([[subQ2,-1.0]])],"derivedFrom":subQ1}),1.0]])]});}
            var Q59;
            {var subQ0=sQuery(id+"F0.wireOp",EDGE,"E55");var subQ1=sQuery(id+"F0.wireOp",EDGE,"E1");var subQ2=makeQuery(id+"F0.imprint","INTERSECT",VERTEX,{"derivedFrom":[subQ1,subQ0]});Q59=makeQuery(id+"F0.imprint","IMPRINT",FACE,{"disambiguationData":[TD([[makeQuery(id+"F0.imprint","IMPRINT",EDGE,{"disambiguationData":[TD([[subQ2,-1.0]])],"derivedFrom":subQ1}),1.0]])]});}
            var Q60;
            {var subQ0=sQuery(id+"F0.wireOp",EDGE,"E22");var subQ1=sQuery(id+"F0.wireOp",EDGE,"E1");var subQ2=makeQuery(id+"F0.imprint","INTERSECT",VERTEX,{"derivedFrom":[subQ1,subQ0]});Q60=makeQuery(id+"F0.imprint","IMPRINT",FACE,{"disambiguationData":[TD([[makeQuery(id+"F0.imprint","IMPRINT",EDGE,{"disambiguationData":[TD([[subQ2,-1.0]])],"derivedFrom":subQ1}),1.0]])]});}
            var Q61;
            {var subQ0=sQuery(id+"F0.wireOp",EDGE,"E52");var subQ1=sQuery(id+"F0.wireOp",EDGE,"E1");var subQ2=makeQuery(id+"F0.imprint","INTERSECT",VERTEX,{"derivedFrom":[subQ1,subQ0]});Q61=makeQuery(id+"F0.imprint","IMPRINT",FACE,{"disambiguationData":[TD([[makeQuery(id+"F0.imprint","IMPRINT",EDGE,{"disambiguationData":[TD([[subQ2,-1.0]])],"derivedFrom":subQ1}),1.0]])]});}
            var Q62;
            {var subQ0=sQuery(id+"F0.wireOp",EDGE,"E21");var subQ1=sQuery(id+"F0.wireOp",EDGE,"E1");var subQ2=makeQuery(id+"F0.imprint","INTERSECT",VERTEX,{"derivedFrom":[subQ1,subQ0]});Q62=makeQuery(id+"F0.imprint","IMPRINT",FACE,{"disambiguationData":[TD([[makeQuery(id+"F0.imprint","IMPRINT",EDGE,{"disambiguationData":[TD([[subQ2,-1.0]])],"derivedFrom":subQ1}),1.0]])]});}
            var Q63;
            {var subQ0=sQuery(id+"F0.wireOp",EDGE,"E49");var subQ1=sQuery(id+"F0.wireOp",EDGE,"E1");var subQ2=makeQuery(id+"F0.imprint","INTERSECT",VERTEX,{"derivedFrom":[subQ1,subQ0]});Q63=makeQuery(id+"F0.imprint","IMPRINT",FACE,{"disambiguationData":[TD([[makeQuery(id+"F0.imprint","IMPRINT",EDGE,{"disambiguationData":[TD([[subQ2,-1.0]])],"derivedFrom":subQ1}),1.0]])]});}
            var Q64;
            {var subQ0=sQuery(id+"F0.wireOp",EDGE,"E20");var subQ1=sQuery(id+"F0.wireOp",EDGE,"E1");var subQ2=makeQuery(id+"F0.imprint","INTERSECT",VERTEX,{"derivedFrom":[subQ1,subQ0]});Q64=makeQuery(id+"F0.imprint","IMPRINT",FACE,{"disambiguationData":[TD([[makeQuery(id+"F0.imprint","IMPRINT",EDGE,{"disambiguationData":[TD([[subQ2,-1.0]])],"derivedFrom":subQ1}),1.0]])]});}
            var Q65;
            {var subQ0=sQuery(id+"F0.wireOp",EDGE,"E46");var subQ1=sQuery(id+"F0.wireOp",EDGE,"E1");var subQ2=makeQuery(id+"F0.imprint","INTERSECT",VERTEX,{"derivedFrom":[subQ1,subQ0]});Q65=makeQuery(id+"F0.imprint","IMPRINT",FACE,{"disambiguationData":[TD([[makeQuery(id+"F0.imprint","IMPRINT",EDGE,{"disambiguationData":[TD([[subQ2,-1.0]])],"derivedFrom":subQ1}),1.0]])]});}
            var Q66;
            {var subQ0=sQuery(id+"F0.wireOp",EDGE,"E19");var subQ1=sQuery(id+"F0.wireOp",EDGE,"E1");var subQ2=makeQuery(id+"F0.imprint","INTERSECT",VERTEX,{"derivedFrom":[subQ1,subQ0]});Q66=makeQuery(id+"F0.imprint","IMPRINT",FACE,{"disambiguationData":[TD([[makeQuery(id+"F0.imprint","IMPRINT",EDGE,{"disambiguationData":[TD([[subQ2,-1.0]])],"derivedFrom":subQ1}),1.0]])]});}
            var Q67;
            {var subQ0=sQuery(id+"F0.wireOp",EDGE,"E43");var subQ1=sQuery(id+"F0.wireOp",EDGE,"E1");var subQ2=makeQuery(id+"F0.imprint","INTERSECT",VERTEX,{"derivedFrom":[subQ1,subQ0]});Q67=makeQuery(id+"F0.imprint","IMPRINT",FACE,{"disambiguationData":[TD([[makeQuery(id+"F0.imprint","IMPRINT",EDGE,{"disambiguationData":[TD([[subQ2,-1.0]])],"derivedFrom":subQ1}),1.0]])]});}
            var Q68;
            {var subQ0=sQuery(id+"F0.wireOp",EDGE,"E18");var subQ1=sQuery(id+"F0.wireOp",EDGE,"E1");var subQ2=makeQuery(id+"F0.imprint","INTERSECT",VERTEX,{"derivedFrom":[subQ1,subQ0]});Q68=makeQuery(id+"F0.imprint","IMPRINT",FACE,{"disambiguationData":[TD([[makeQuery(id+"F0.imprint","IMPRINT",EDGE,{"disambiguationData":[TD([[subQ2,-1.0]])],"derivedFrom":subQ1}),1.0]])]});}
            var Q69;
            {var subQ0=sQuery(id+"F0.wireOp",EDGE,"E40");var subQ1=sQuery(id+"F0.wireOp",EDGE,"E1");var subQ2=makeQuery(id+"F0.imprint","INTERSECT",VERTEX,{"derivedFrom":[subQ1,subQ0]});Q69=makeQuery(id+"F0.imprint","IMPRINT",FACE,{"disambiguationData":[TD([[makeQuery(id+"F0.imprint","IMPRINT",EDGE,{"disambiguationData":[TD([[subQ2,-1.0]])],"derivedFrom":subQ1}),1.0]])]});}
            var Q70;
            {var subQ0=sQuery(id+"F0.wireOp",EDGE,"E17");var subQ1=sQuery(id+"F0.wireOp",EDGE,"E1");var subQ2=makeQuery(id+"F0.imprint","INTERSECT",VERTEX,{"derivedFrom":[subQ1,subQ0]});Q70=makeQuery(id+"F0.imprint","IMPRINT",FACE,{"disambiguationData":[TD([[makeQuery(id+"F0.imprint","IMPRINT",EDGE,{"disambiguationData":[TD([[subQ2,-1.0]])],"derivedFrom":subQ1}),1.0]])]});}
            var Q71;
            {var subQ0=sQuery(id+"F0.wireOp",EDGE,"E37");var subQ1=sQuery(id+"F0.wireOp",EDGE,"E1");var subQ2=makeQuery(id+"F0.imprint","INTERSECT",VERTEX,{"derivedFrom":[subQ1,subQ0]});Q71=makeQuery(id+"F0.imprint","IMPRINT",FACE,{"disambiguationData":[TD([[makeQuery(id+"F0.imprint","IMPRINT",EDGE,{"disambiguationData":[TD([[subQ2,-1.0]])],"derivedFrom":subQ1}),1.0]])]});}
            var Q72;
            {var subQ0=sQuery(id+"F0.wireOp",EDGE,"E16");var subQ1=sQuery(id+"F0.wireOp",EDGE,"E1");var subQ2=makeQuery(id+"F0.imprint","INTERSECT",VERTEX,{"derivedFrom":[subQ1,subQ0]});Q72=makeQuery(id+"F0.imprint","IMPRINT",FACE,{"disambiguationData":[TD([[makeQuery(id+"F0.imprint","IMPRINT",EDGE,{"disambiguationData":[TD([[subQ2,-1.0]])],"derivedFrom":subQ1}),1.0]])]});}
            var Q73;
            {var subQ0=sQuery(id+"F0.wireOp",EDGE,"E34");var subQ1=sQuery(id+"F0.wireOp",EDGE,"E1");var subQ2=makeQuery(id+"F0.imprint","INTERSECT",VERTEX,{"derivedFrom":[subQ1,subQ0]});Q73=makeQuery(id+"F0.imprint","IMPRINT",FACE,{"disambiguationData":[TD([[makeQuery(id+"F0.imprint","IMPRINT",EDGE,{"disambiguationData":[TD([[subQ2,-1.0]])],"derivedFrom":subQ1}),1.0]])]});}
            var Q74;
            {var subQ0=sQuery(id+"F0.wireOp",EDGE,"E15");var subQ1=sQuery(id+"F0.wireOp",EDGE,"E1");var subQ2=makeQuery(id+"F0.imprint","INTERSECT",VERTEX,{"derivedFrom":[subQ1,subQ0]});Q74=makeQuery(id+"F0.imprint","IMPRINT",FACE,{"disambiguationData":[TD([[makeQuery(id+"F0.imprint","IMPRINT",EDGE,{"disambiguationData":[TD([[subQ2,-1.0]])],"derivedFrom":subQ1}),1.0]])]});}
            var Q75;
            {var subQ0=sQuery(id+"F0.wireOp",EDGE,"E31");var subQ1=sQuery(id+"F0.wireOp",EDGE,"E1");var subQ2=makeQuery(id+"F0.imprint","INTERSECT",VERTEX,{"derivedFrom":[subQ1,subQ0]});Q75=makeQuery(id+"F0.imprint","IMPRINT",FACE,{"disambiguationData":[TD([[makeQuery(id+"F0.imprint","IMPRINT",EDGE,{"disambiguationData":[TD([[subQ2,-1.0]])],"derivedFrom":subQ1}),1.0]])]});}
            var Q76;
            {var subQ0=sQuery(id+"F0.wireOp",EDGE,"E14");var subQ1=sQuery(id+"F0.wireOp",EDGE,"E1");var subQ2=makeQuery(id+"F0.imprint","INTERSECT",VERTEX,{"derivedFrom":[subQ1,subQ0]});Q76=makeQuery(id+"F0.imprint","IMPRINT",FACE,{"disambiguationData":[TD([[makeQuery(id+"F0.imprint","IMPRINT",EDGE,{"disambiguationData":[TD([[subQ2,-1.0]])],"derivedFrom":subQ1}),1.0]])]});}
            var Q77;
            {var subQ0=sQuery(id+"F0.wireOp",EDGE,"E11");var subQ1=sQuery(id+"F0.wireOp",EDGE,"E1");var subQ2=makeQuery(id+"F0.imprint","INTERSECT",VERTEX,{"derivedFrom":[subQ1,subQ0]});Q77=makeQuery(id+"F0.imprint","IMPRINT",FACE,{"disambiguationData":[TD([[makeQuery(id+"F0.imprint","IMPRINT",EDGE,{"disambiguationData":[TD([[subQ2,-1.0]])],"derivedFrom":subQ1}),1.0]])]});}
            var Q78;
            {var subQ0=sQuery(id+"F0.wireOp",EDGE,"E9");var subQ1=sQuery(id+"F0.wireOp",EDGE,"E1");var subQ2=makeQuery(id+"F0.imprint","INTERSECT",VERTEX,{"derivedFrom":[subQ1,subQ0]});Q78=makeQuery(id+"F0.imprint","IMPRINT",FACE,{"disambiguationData":[TD([[makeQuery(id+"F0.imprint","IMPRINT",EDGE,{"disambiguationData":[TD([[subQ2,-1.0]])],"derivedFrom":subQ1}),1.0]])]});}
            var Q79;
            {var subQ0=sQuery(id+"F0.wireOp",EDGE,"E7");var subQ1=sQuery(id+"F0.wireOp",EDGE,"E1");var subQ2=makeQuery(id+"F0.imprint","INTERSECT",VERTEX,{"derivedFrom":[subQ1,subQ0]});Q79=makeQuery(id+"F0.imprint","IMPRINT",FACE,{"disambiguationData":[TD([[makeQuery(id+"F0.imprint","IMPRINT",EDGE,{"disambiguationData":[TD([[subQ2,-1.0]])],"derivedFrom":subQ1}),1.0]])]});}
            var Q80;
            {var subQ0=sQuery(id+"F0.wireOp",EDGE,"E2");var subQ1=sQuery(id+"F0.wireOp",EDGE,"E1");var subQ2=makeQuery(id+"F0.imprint","INTERSECT",VERTEX,{"derivedFrom":[subQ1,subQ0]});Q80=makeQuery(id+"F0.imprint","IMPRINT",FACE,{"disambiguationData":[TD([[makeQuery(id+"F0.imprint","IMPRINT",EDGE,{"disambiguationData":[TD([[subQ2,-1.0]])],"derivedFrom":subQ1}),1.0]])]});}
            var Q81;
            {var subQ0=sQuery(id+"F0.wireOp",EDGE,"E103");var subQ1=sQuery(id+"F0.wireOp",EDGE,"E1");var subQ2=makeQuery(id+"F0.imprint","INTERSECT",VERTEX,{"derivedFrom":[subQ1,subQ0]});Q81=makeQuery(id+"F0.imprint","IMPRINT",FACE,{"disambiguationData":[TD([[makeQuery(id+"F0.imprint","IMPRINT",EDGE,{"disambiguationData":[TD([[subQ2,1.0]])],"derivedFrom":subQ1}),1.0]])]});}
            var Q82;
            {var subQ0=sQuery(id+"F0.wireOp",EDGE,"E103");var subQ1=sQuery(id+"F0.wireOp",EDGE,"E1");var subQ2=makeQuery(id+"F0.imprint","INTERSECT",VERTEX,{"derivedFrom":[subQ1,subQ0]});Q82=makeQuery(id+"F0.imprint","IMPRINT",FACE,{"disambiguationData":[TD([[makeQuery(id+"F0.imprint","IMPRINT",EDGE,{"disambiguationData":[TD([[subQ2,-1.0]])],"derivedFrom":subQ1}),1.0]])]});}
            var Q83;
            {var subQ0=sQuery(id+"F0.wireOp",EDGE,"E107");var subQ1=sQuery(id+"F0.wireOp",EDGE,"E1");var subQ2=makeQuery(id+"F0.imprint","INTERSECT",VERTEX,{"derivedFrom":[subQ1,subQ0]});Q83=makeQuery(id+"F0.imprint","IMPRINT",FACE,{"disambiguationData":[TD([[makeQuery(id+"F0.imprint","IMPRINT",EDGE,{"disambiguationData":[TD([[subQ2,-1.0]])],"derivedFrom":subQ1}),1.0]])]});}
            var Q84;
            {var subQ0=sQuery(id+"F0.wireOp",EDGE,"E113");var subQ1=sQuery(id+"F0.wireOp",EDGE,"E1");var subQ2=makeQuery(id+"F0.imprint","INTERSECT",VERTEX,{"derivedFrom":[subQ1,subQ0]});Q84=makeQuery(id+"F0.imprint","IMPRINT",FACE,{"disambiguationData":[TD([[makeQuery(id+"F0.imprint","IMPRINT",EDGE,{"disambiguationData":[TD([[subQ2,-1.0]])],"derivedFrom":subQ1}),1.0]])]});}
            var Q85;
            {var subQ0=sQuery(id+"F0.wireOp",EDGE,"E110");var subQ1=sQuery(id+"F0.wireOp",EDGE,"E1");var subQ2=makeQuery(id+"F0.imprint","INTERSECT",VERTEX,{"derivedFrom":[subQ1,subQ0]});Q85=makeQuery(id+"F0.imprint","IMPRINT",FACE,{"disambiguationData":[TD([[makeQuery(id+"F0.imprint","IMPRINT",EDGE,{"disambiguationData":[TD([[subQ2,-1.0]])],"derivedFrom":subQ1}),1.0]])]});}
            extrude(context, id + "F1", {"entities" : qUnion([Q0, Q1, Q2, Q3, Q4, Q5, Q6, Q7, Q8, Q9, Q10, Q11, Q12, Q13, Q14, Q15, Q16, Q17, Q18, Q19, Q20, Q21, Q22, Q23, Q24, Q25, Q26, Q27, Q28, Q29, Q30, Q31, Q32, Q33, Q34, Q35, Q36, Q37, Q38, Q39, Q40, Q41, Q42, Q43, Q44, Q45, Q46, Q47, Q48, Q49, Q50, Q51, Q52, Q53, Q54, Q55, Q56, Q57, Q58, Q59, Q60, Q61, Q62, Q63, Q64, Q65, Q66, Q67, Q68, Q69, Q70, Q71, Q72, Q73, Q74, Q75, Q76, Q77, Q78, Q79, Q80, Q81, Q82, Q83, Q84, Q85]), "depth" : 3 * mm, "offsetDistance" : 25 * mm});
        }
        {
            var Q0;
            {var subQ5=sQuery(id+"F0.wireOp",EDGE,"E95");Q0=makeQuery(id+"F0.imprint","IMPRINT",FACE,{"disambiguationData":[TD([[makeQuery(id+"F0.imprint","IMPRINT",EDGE,{"derivedFrom":subQ5}),1.0]])]});}
            var Q1;
            {var subQ5=sQuery(id+"F0.wireOp",EDGE,"E75");Q1=makeQuery(id+"F0.imprint","IMPRINT",FACE,{"disambiguationData":[TD([[makeQuery(id+"F0.imprint","IMPRINT",EDGE,{"derivedFrom":subQ5}),1.0]])]});}
            var Q2;
            {var subQ5=sQuery(id+"F0.wireOp",EDGE,"E72");Q2=makeQuery(id+"F0.imprint","IMPRINT",FACE,{"disambiguationData":[TD([[makeQuery(id+"F0.imprint","IMPRINT",EDGE,{"derivedFrom":subQ5}),1.0]])]});}
            var Q3;
            {var subQ5=sQuery(id+"F0.wireOp",EDGE,"E69");Q3=makeQuery(id+"F0.imprint","IMPRINT",FACE,{"disambiguationData":[TD([[makeQuery(id+"F0.imprint","IMPRINT",EDGE,{"derivedFrom":subQ5}),1.0]])]});}
            var Q4;
            {var subQ5=sQuery(id+"F0.wireOp",EDGE,"E66");Q4=makeQuery(id+"F0.imprint","IMPRINT",FACE,{"disambiguationData":[TD([[makeQuery(id+"F0.imprint","IMPRINT",EDGE,{"derivedFrom":subQ5}),1.0]])]});}
            var Q5;
            {var subQ5=sQuery(id+"F0.wireOp",EDGE,"E63");Q5=makeQuery(id+"F0.imprint","IMPRINT",FACE,{"disambiguationData":[TD([[makeQuery(id+"F0.imprint","IMPRINT",EDGE,{"derivedFrom":subQ5}),1.0]])]});}
            var Q6;
            {var subQ5=sQuery(id+"F0.wireOp",EDGE,"E60");Q6=makeQuery(id+"F0.imprint","IMPRINT",FACE,{"disambiguationData":[TD([[makeQuery(id+"F0.imprint","IMPRINT",EDGE,{"derivedFrom":subQ5}),1.0]])]});}
            var Q7;
            {var subQ5=sQuery(id+"F0.wireOp",EDGE,"E57");Q7=makeQuery(id+"F0.imprint","IMPRINT",FACE,{"disambiguationData":[TD([[makeQuery(id+"F0.imprint","IMPRINT",EDGE,{"derivedFrom":subQ5}),1.0]])]});}
            var Q8;
            {var subQ5=sQuery(id+"F0.wireOp",EDGE,"E54");Q8=makeQuery(id+"F0.imprint","IMPRINT",FACE,{"disambiguationData":[TD([[makeQuery(id+"F0.imprint","IMPRINT",EDGE,{"derivedFrom":subQ5}),1.0]])]});}
            var Q9;
            {var subQ5=sQuery(id+"F0.wireOp",EDGE,"E51");Q9=makeQuery(id+"F0.imprint","IMPRINT",FACE,{"disambiguationData":[TD([[makeQuery(id+"F0.imprint","IMPRINT",EDGE,{"derivedFrom":subQ5}),1.0]])]});}
            var Q10;
            {var subQ5=sQuery(id+"F0.wireOp",EDGE,"E48");Q10=makeQuery(id+"F0.imprint","IMPRINT",FACE,{"disambiguationData":[TD([[makeQuery(id+"F0.imprint","IMPRINT",EDGE,{"derivedFrom":subQ5}),1.0]])]});}
            var Q11;
            {var subQ5=sQuery(id+"F0.wireOp",EDGE,"E45");Q11=makeQuery(id+"F0.imprint","IMPRINT",FACE,{"disambiguationData":[TD([[makeQuery(id+"F0.imprint","IMPRINT",EDGE,{"derivedFrom":subQ5}),1.0]])]});}
            var Q12;
            {var subQ0=sQuery(id+"F0.wireOp",EDGE,"E19");var subQ1=sQuery(id+"F0.wireOp",EDGE,"E0");var subQ2=makeQuery(id+"F0.imprint","INTERSECT",VERTEX,{"derivedFrom":[subQ1,subQ0]});Q12=makeQuery(id+"F0.imprint","IMPRINT",FACE,{"disambiguationData":[TD([[makeQuery(id+"F0.imprint","IMPRINT",EDGE,{"disambiguationData":[TD([[subQ2,-1.0]])],"derivedFrom":subQ1}),1.0]])]});}
            var Q13;
            {var subQ5=sQuery(id+"F0.wireOp",EDGE,"E97");Q13=makeQuery(id+"F0.imprint","IMPRINT",FACE,{"disambiguationData":[TD([[makeQuery(id+"F0.imprint","IMPRINT",EDGE,{"derivedFrom":subQ5}),1.0]])]});}
            var Q14;
            {var subQ5=sQuery(id+"F0.wireOp",EDGE,"E77");Q14=makeQuery(id+"F0.imprint","IMPRINT",FACE,{"disambiguationData":[TD([[makeQuery(id+"F0.imprint","IMPRINT",EDGE,{"derivedFrom":subQ5}),1.0]])]});}
            var Q15;
            {var subQ5=sQuery(id+"F0.wireOp",EDGE,"E74");Q15=makeQuery(id+"F0.imprint","IMPRINT",FACE,{"disambiguationData":[TD([[makeQuery(id+"F0.imprint","IMPRINT",EDGE,{"derivedFrom":subQ5}),1.0]])]});}
            var Q16;
            {var subQ5=sQuery(id+"F0.wireOp",EDGE,"E71");Q16=makeQuery(id+"F0.imprint","IMPRINT",FACE,{"disambiguationData":[TD([[makeQuery(id+"F0.imprint","IMPRINT",EDGE,{"derivedFrom":subQ5}),1.0]])]});}
            var Q17;
            {var subQ5=sQuery(id+"F0.wireOp",EDGE,"E68");Q17=makeQuery(id+"F0.imprint","IMPRINT",FACE,{"disambiguationData":[TD([[makeQuery(id+"F0.imprint","IMPRINT",EDGE,{"derivedFrom":subQ5}),1.0]])]});}
            var Q18;
            {var subQ5=sQuery(id+"F0.wireOp",EDGE,"E65");Q18=makeQuery(id+"F0.imprint","IMPRINT",FACE,{"disambiguationData":[TD([[makeQuery(id+"F0.imprint","IMPRINT",EDGE,{"derivedFrom":subQ5}),1.0]])]});}
            var Q19;
            {var subQ5=sQuery(id+"F0.wireOp",EDGE,"E62");Q19=makeQuery(id+"F0.imprint","IMPRINT",FACE,{"disambiguationData":[TD([[makeQuery(id+"F0.imprint","IMPRINT",EDGE,{"derivedFrom":subQ5}),1.0]])]});}
            var Q20;
            {var subQ5=sQuery(id+"F0.wireOp",EDGE,"E59");Q20=makeQuery(id+"F0.imprint","IMPRINT",FACE,{"disambiguationData":[TD([[makeQuery(id+"F0.imprint","IMPRINT",EDGE,{"derivedFrom":subQ5}),1.0]])]});}
            var Q21;
            {var subQ5=sQuery(id+"F0.wireOp",EDGE,"E56");Q21=makeQuery(id+"F0.imprint","IMPRINT",FACE,{"disambiguationData":[TD([[makeQuery(id+"F0.imprint","IMPRINT",EDGE,{"derivedFrom":subQ5}),1.0]])]});}
            var Q22;
            {var subQ5=sQuery(id+"F0.wireOp",EDGE,"E53");Q22=makeQuery(id+"F0.imprint","IMPRINT",FACE,{"disambiguationData":[TD([[makeQuery(id+"F0.imprint","IMPRINT",EDGE,{"derivedFrom":subQ5}),1.0]])]});}
            var Q23;
            {var subQ5=sQuery(id+"F0.wireOp",EDGE,"E50");Q23=makeQuery(id+"F0.imprint","IMPRINT",FACE,{"disambiguationData":[TD([[makeQuery(id+"F0.imprint","IMPRINT",EDGE,{"derivedFrom":subQ5}),1.0]])]});}
            var Q24;
            {var subQ5=sQuery(id+"F0.wireOp",EDGE,"E47");Q24=makeQuery(id+"F0.imprint","IMPRINT",FACE,{"disambiguationData":[TD([[makeQuery(id+"F0.imprint","IMPRINT",EDGE,{"derivedFrom":subQ5}),1.0]])]});}
            var Q25;
            {var subQ0=sQuery(id+"F0.wireOp",EDGE,"E94");var subQ1=sQuery(id+"F0.wireOp",EDGE,"E0");var subQ2=makeQuery(id+"F0.imprint","INTERSECT",VERTEX,{"derivedFrom":[subQ1,subQ0]});Q25=makeQuery(id+"F0.imprint","IMPRINT",FACE,{"disambiguationData":[TD([[makeQuery(id+"F0.imprint","IMPRINT",EDGE,{"disambiguationData":[TD([[subQ2,-1.0]])],"derivedFrom":subQ1}),1.0]])]});}
            var Q26;
            {var subQ0=sQuery(id+"F0.wireOp",EDGE,"E29");var subQ1=sQuery(id+"F0.wireOp",EDGE,"E0");var subQ2=makeQuery(id+"F0.imprint","INTERSECT",VERTEX,{"derivedFrom":[subQ1,subQ0]});Q26=makeQuery(id+"F0.imprint","IMPRINT",FACE,{"disambiguationData":[TD([[makeQuery(id+"F0.imprint","IMPRINT",EDGE,{"disambiguationData":[TD([[subQ2,-1.0]])],"derivedFrom":subQ1}),1.0]])]});}
            var Q27;
            {var subQ0=sQuery(id+"F0.wireOp",EDGE,"E28");var subQ1=sQuery(id+"F0.wireOp",EDGE,"E0");var subQ2=makeQuery(id+"F0.imprint","INTERSECT",VERTEX,{"derivedFrom":[subQ1,subQ0]});Q27=makeQuery(id+"F0.imprint","IMPRINT",FACE,{"disambiguationData":[TD([[makeQuery(id+"F0.imprint","IMPRINT",EDGE,{"disambiguationData":[TD([[subQ2,-1.0]])],"derivedFrom":subQ1}),1.0]])]});}
            var Q28;
            {var subQ0=sQuery(id+"F0.wireOp",EDGE,"E27");var subQ1=sQuery(id+"F0.wireOp",EDGE,"E0");var subQ2=makeQuery(id+"F0.imprint","INTERSECT",VERTEX,{"derivedFrom":[subQ1,subQ0]});Q28=makeQuery(id+"F0.imprint","IMPRINT",FACE,{"disambiguationData":[TD([[makeQuery(id+"F0.imprint","IMPRINT",EDGE,{"disambiguationData":[TD([[subQ2,-1.0]])],"derivedFrom":subQ1}),1.0]])]});}
            var Q29;
            {var subQ0=sQuery(id+"F0.wireOp",EDGE,"E26");var subQ1=sQuery(id+"F0.wireOp",EDGE,"E0");var subQ2=makeQuery(id+"F0.imprint","INTERSECT",VERTEX,{"derivedFrom":[subQ1,subQ0]});Q29=makeQuery(id+"F0.imprint","IMPRINT",FACE,{"disambiguationData":[TD([[makeQuery(id+"F0.imprint","IMPRINT",EDGE,{"disambiguationData":[TD([[subQ2,-1.0]])],"derivedFrom":subQ1}),1.0]])]});}
            var Q30;
            {var subQ0=sQuery(id+"F0.wireOp",EDGE,"E25");var subQ1=sQuery(id+"F0.wireOp",EDGE,"E0");var subQ2=makeQuery(id+"F0.imprint","INTERSECT",VERTEX,{"derivedFrom":[subQ1,subQ0]});Q30=makeQuery(id+"F0.imprint","IMPRINT",FACE,{"disambiguationData":[TD([[makeQuery(id+"F0.imprint","IMPRINT",EDGE,{"disambiguationData":[TD([[subQ2,-1.0]])],"derivedFrom":subQ1}),1.0]])]});}
            var Q31;
            {var subQ0=sQuery(id+"F0.wireOp",EDGE,"E24");var subQ1=sQuery(id+"F0.wireOp",EDGE,"E0");var subQ2=makeQuery(id+"F0.imprint","INTERSECT",VERTEX,{"derivedFrom":[subQ1,subQ0]});Q31=makeQuery(id+"F0.imprint","IMPRINT",FACE,{"disambiguationData":[TD([[makeQuery(id+"F0.imprint","IMPRINT",EDGE,{"disambiguationData":[TD([[subQ2,-1.0]])],"derivedFrom":subQ1}),1.0]])]});}
            var Q32;
            {var subQ0=sQuery(id+"F0.wireOp",EDGE,"E23");var subQ1=sQuery(id+"F0.wireOp",EDGE,"E0");var subQ2=makeQuery(id+"F0.imprint","INTERSECT",VERTEX,{"derivedFrom":[subQ1,subQ0]});Q32=makeQuery(id+"F0.imprint","IMPRINT",FACE,{"disambiguationData":[TD([[makeQuery(id+"F0.imprint","IMPRINT",EDGE,{"disambiguationData":[TD([[subQ2,-1.0]])],"derivedFrom":subQ1}),1.0]])]});}
            var Q33;
            {var subQ0=sQuery(id+"F0.wireOp",EDGE,"E22");var subQ1=sQuery(id+"F0.wireOp",EDGE,"E0");var subQ2=makeQuery(id+"F0.imprint","INTERSECT",VERTEX,{"derivedFrom":[subQ1,subQ0]});Q33=makeQuery(id+"F0.imprint","IMPRINT",FACE,{"disambiguationData":[TD([[makeQuery(id+"F0.imprint","IMPRINT",EDGE,{"disambiguationData":[TD([[subQ2,-1.0]])],"derivedFrom":subQ1}),1.0]])]});}
            var Q34;
            {var subQ0=sQuery(id+"F0.wireOp",EDGE,"E21");var subQ1=sQuery(id+"F0.wireOp",EDGE,"E0");var subQ2=makeQuery(id+"F0.imprint","INTERSECT",VERTEX,{"derivedFrom":[subQ1,subQ0]});Q34=makeQuery(id+"F0.imprint","IMPRINT",FACE,{"disambiguationData":[TD([[makeQuery(id+"F0.imprint","IMPRINT",EDGE,{"disambiguationData":[TD([[subQ2,-1.0]])],"derivedFrom":subQ1}),1.0]])]});}
            var Q35;
            {var subQ0=sQuery(id+"F0.wireOp",EDGE,"E20");var subQ1=sQuery(id+"F0.wireOp",EDGE,"E0");var subQ2=makeQuery(id+"F0.imprint","INTERSECT",VERTEX,{"derivedFrom":[subQ1,subQ0]});Q35=makeQuery(id+"F0.imprint","IMPRINT",FACE,{"disambiguationData":[TD([[makeQuery(id+"F0.imprint","IMPRINT",EDGE,{"disambiguationData":[TD([[subQ2,-1.0]])],"derivedFrom":subQ1}),1.0]])]});}
            var Q36;
            {var subQ5=sQuery(id+"F0.wireOp",EDGE,"E44");Q36=makeQuery(id+"F0.imprint","IMPRINT",FACE,{"disambiguationData":[TD([[makeQuery(id+"F0.imprint","IMPRINT",EDGE,{"derivedFrom":subQ5}),1.0]])]});}
            var Q37;
            {var subQ5=sQuery(id+"F0.wireOp",EDGE,"E41");Q37=makeQuery(id+"F0.imprint","IMPRINT",FACE,{"disambiguationData":[TD([[makeQuery(id+"F0.imprint","IMPRINT",EDGE,{"derivedFrom":subQ5}),1.0]])]});}
            var Q38;
            {var subQ5=sQuery(id+"F0.wireOp",EDGE,"E38");Q38=makeQuery(id+"F0.imprint","IMPRINT",FACE,{"disambiguationData":[TD([[makeQuery(id+"F0.imprint","IMPRINT",EDGE,{"derivedFrom":subQ5}),1.0]])]});}
            var Q39;
            {var subQ5=sQuery(id+"F0.wireOp",EDGE,"E35");Q39=makeQuery(id+"F0.imprint","IMPRINT",FACE,{"disambiguationData":[TD([[makeQuery(id+"F0.imprint","IMPRINT",EDGE,{"derivedFrom":subQ5}),1.0]])]});}
            var Q40;
            {var subQ5=sQuery(id+"F0.wireOp",EDGE,"E32");Q40=makeQuery(id+"F0.imprint","IMPRINT",FACE,{"disambiguationData":[TD([[makeQuery(id+"F0.imprint","IMPRINT",EDGE,{"derivedFrom":subQ5}),1.0]])]});}
            var Q41;
            {var subQ5=sQuery(id+"F0.wireOp",EDGE,"E12");Q41=makeQuery(id+"F0.imprint","IMPRINT",FACE,{"disambiguationData":[TD([[makeQuery(id+"F0.imprint","IMPRINT",EDGE,{"derivedFrom":subQ5}),1.0]])]});}
            var Q42;
            {var subQ0=sQuery(id+"F0.wireOp",EDGE,"E8");Q42=makeQuery(id+"F0.imprint","IMPRINT",FACE,{"disambiguationData":[TD([[makeQuery(id+"F0.imprint","IMPRINT",EDGE,{"derivedFrom":subQ0}),1.0]])]});}
            var Q43;
            {var subQ0=sQuery(id+"F0.wireOp",EDGE,"E6");Q43=makeQuery(id+"F0.imprint","IMPRINT",FACE,{"disambiguationData":[TD([[makeQuery(id+"F0.imprint","IMPRINT",EDGE,{"derivedFrom":subQ0}),1.0]])]});}
            var Q44;
            {var subQ5=sQuery(id+"F0.wireOp",EDGE,"E10");Q44=makeQuery(id+"F0.imprint","IMPRINT",FACE,{"disambiguationData":[TD([[makeQuery(id+"F0.imprint","IMPRINT",EDGE,{"derivedFrom":subQ5}),1.0]])]});}
            var Q45;
            {var subQ5=sQuery(id+"F0.wireOp",EDGE,"E30");Q45=makeQuery(id+"F0.imprint","IMPRINT",FACE,{"disambiguationData":[TD([[makeQuery(id+"F0.imprint","IMPRINT",EDGE,{"derivedFrom":subQ5}),1.0]])]});}
            var Q46;
            {var subQ5=sQuery(id+"F0.wireOp",EDGE,"E33");Q46=makeQuery(id+"F0.imprint","IMPRINT",FACE,{"disambiguationData":[TD([[makeQuery(id+"F0.imprint","IMPRINT",EDGE,{"derivedFrom":subQ5}),1.0]])]});}
            var Q47;
            {var subQ5=sQuery(id+"F0.wireOp",EDGE,"E36");Q47=makeQuery(id+"F0.imprint","IMPRINT",FACE,{"disambiguationData":[TD([[makeQuery(id+"F0.imprint","IMPRINT",EDGE,{"derivedFrom":subQ5}),1.0]])]});}
            var Q48;
            {var subQ5=sQuery(id+"F0.wireOp",EDGE,"E39");Q48=makeQuery(id+"F0.imprint","IMPRINT",FACE,{"disambiguationData":[TD([[makeQuery(id+"F0.imprint","IMPRINT",EDGE,{"derivedFrom":subQ5}),1.0]])]});}
            var Q49;
            {var subQ5=sQuery(id+"F0.wireOp",EDGE,"E42");Q49=makeQuery(id+"F0.imprint","IMPRINT",FACE,{"disambiguationData":[TD([[makeQuery(id+"F0.imprint","IMPRINT",EDGE,{"derivedFrom":subQ5}),1.0]])]});}
            var Q50;
            {var subQ0=sQuery(id+"F0.wireOp",EDGE,"E18");var subQ1=sQuery(id+"F0.wireOp",EDGE,"E0");var subQ2=makeQuery(id+"F0.imprint","INTERSECT",VERTEX,{"derivedFrom":[subQ1,subQ0]});Q50=makeQuery(id+"F0.imprint","IMPRINT",FACE,{"disambiguationData":[TD([[makeQuery(id+"F0.imprint","IMPRINT",EDGE,{"disambiguationData":[TD([[subQ2,-1.0]])],"derivedFrom":subQ1}),1.0]])]});}
            var Q51;
            {var subQ0=sQuery(id+"F0.wireOp",EDGE,"E17");var subQ1=sQuery(id+"F0.wireOp",EDGE,"E0");var subQ2=makeQuery(id+"F0.imprint","INTERSECT",VERTEX,{"derivedFrom":[subQ1,subQ0]});Q51=makeQuery(id+"F0.imprint","IMPRINT",FACE,{"disambiguationData":[TD([[makeQuery(id+"F0.imprint","IMPRINT",EDGE,{"disambiguationData":[TD([[subQ2,-1.0]])],"derivedFrom":subQ1}),1.0]])]});}
            var Q52;
            {var subQ0=sQuery(id+"F0.wireOp",EDGE,"E16");var subQ1=sQuery(id+"F0.wireOp",EDGE,"E0");var subQ2=makeQuery(id+"F0.imprint","INTERSECT",VERTEX,{"derivedFrom":[subQ1,subQ0]});Q52=makeQuery(id+"F0.imprint","IMPRINT",FACE,{"disambiguationData":[TD([[makeQuery(id+"F0.imprint","IMPRINT",EDGE,{"disambiguationData":[TD([[subQ2,-1.0]])],"derivedFrom":subQ1}),1.0]])]});}
            var Q53;
            {var subQ0=sQuery(id+"F0.wireOp",EDGE,"E15");var subQ1=sQuery(id+"F0.wireOp",EDGE,"E0");var subQ2=makeQuery(id+"F0.imprint","INTERSECT",VERTEX,{"derivedFrom":[subQ1,subQ0]});Q53=makeQuery(id+"F0.imprint","IMPRINT",FACE,{"disambiguationData":[TD([[makeQuery(id+"F0.imprint","IMPRINT",EDGE,{"disambiguationData":[TD([[subQ2,-1.0]])],"derivedFrom":subQ1}),1.0]])]});}
            var Q54;
            {var subQ0=sQuery(id+"F0.wireOp",EDGE,"E14");var subQ1=sQuery(id+"F0.wireOp",EDGE,"E0");var subQ2=makeQuery(id+"F0.imprint","INTERSECT",VERTEX,{"derivedFrom":[subQ1,subQ0]});Q54=makeQuery(id+"F0.imprint","IMPRINT",FACE,{"disambiguationData":[TD([[makeQuery(id+"F0.imprint","IMPRINT",EDGE,{"disambiguationData":[TD([[subQ2,-1.0]])],"derivedFrom":subQ1}),1.0]])]});}
            var Q55;
            {var subQ0=sQuery(id+"F0.wireOp",EDGE,"E9");var subQ1=sQuery(id+"F0.wireOp",EDGE,"E0");var subQ2=makeQuery(id+"F0.imprint","INTERSECT",VERTEX,{"derivedFrom":[subQ1,subQ0]});Q55=makeQuery(id+"F0.imprint","IMPRINT",FACE,{"disambiguationData":[TD([[makeQuery(id+"F0.imprint","IMPRINT",EDGE,{"disambiguationData":[TD([[subQ2,-1.0]])],"derivedFrom":subQ1}),1.0]])]});}
            var Q56;
            {var subQ0=sQuery(id+"F0.wireOp",EDGE,"E2");var subQ1=sQuery(id+"F0.wireOp",EDGE,"E0");var subQ2=makeQuery(id+"F0.imprint","INTERSECT",VERTEX,{"derivedFrom":[subQ1,subQ0]});Q56=makeQuery(id+"F0.imprint","IMPRINT",FACE,{"disambiguationData":[TD([[makeQuery(id+"F0.imprint","IMPRINT",EDGE,{"disambiguationData":[TD([[subQ2,-1.0]])],"derivedFrom":subQ1}),1.0]])]});}
            var Q57;
            {var subQ0=sQuery(id+"F0.wireOp",EDGE,"E107");var subQ1=sQuery(id+"F0.wireOp",EDGE,"E0");var subQ2=makeQuery(id+"F0.imprint","INTERSECT",VERTEX,{"derivedFrom":[subQ1,subQ0]});Q57=makeQuery(id+"F0.imprint","IMPRINT",FACE,{"disambiguationData":[TD([[makeQuery(id+"F0.imprint","IMPRINT",EDGE,{"disambiguationData":[TD([[subQ2,-1.0]])],"derivedFrom":subQ1}),1.0]])]});}
            var Q58;
            {var subQ5=sQuery(id+"F0.wireOp",EDGE,"E112");Q58=makeQuery(id+"F0.imprint","IMPRINT",FACE,{"disambiguationData":[TD([[makeQuery(id+"F0.imprint","IMPRINT",EDGE,{"derivedFrom":subQ5}),1.0]])]});}
            var Q59;
            {var subQ5=sQuery(id+"F0.wireOp",EDGE,"E109");Q59=makeQuery(id+"F0.imprint","IMPRINT",FACE,{"disambiguationData":[TD([[makeQuery(id+"F0.imprint","IMPRINT",EDGE,{"derivedFrom":subQ5}),1.0]])]});}
            var Q60;
            {var subQ0=sQuery(id+"F0.wireOp",EDGE,"E110");var subQ1=sQuery(id+"F0.wireOp",EDGE,"E0");var subQ2=makeQuery(id+"F0.imprint","INTERSECT",VERTEX,{"derivedFrom":[subQ1,subQ0]});Q60=makeQuery(id+"F0.imprint","IMPRINT",FACE,{"disambiguationData":[TD([[makeQuery(id+"F0.imprint","IMPRINT",EDGE,{"disambiguationData":[TD([[subQ2,-1.0]])],"derivedFrom":subQ1}),1.0]])]});}
            var Q61;
            {var subQ5=sQuery(id+"F0.wireOp",EDGE,"E111");Q61=makeQuery(id+"F0.imprint","IMPRINT",FACE,{"disambiguationData":[TD([[makeQuery(id+"F0.imprint","IMPRINT",EDGE,{"derivedFrom":subQ5}),1.0]])]});}
            var Q62;
            {var subQ5=sQuery(id+"F0.wireOp",EDGE,"E114");Q62=makeQuery(id+"F0.imprint","IMPRINT",FACE,{"disambiguationData":[TD([[makeQuery(id+"F0.imprint","IMPRINT",EDGE,{"derivedFrom":subQ5}),1.0]])]});}
            var Q63;
            {var subQ0=sQuery(id+"F0.wireOp",EDGE,"E103");var subQ1=sQuery(id+"F0.wireOp",EDGE,"E0");var subQ2=makeQuery(id+"F0.imprint","INTERSECT",VERTEX,{"derivedFrom":[subQ1,subQ0]});Q63=makeQuery(id+"F0.imprint","IMPRINT",FACE,{"disambiguationData":[TD([[makeQuery(id+"F0.imprint","IMPRINT",EDGE,{"disambiguationData":[TD([[subQ2,1.0]])],"derivedFrom":subQ1}),1.0]])]});}
            var Q64;
            {var subQ5=sQuery(id+"F0.wireOp",EDGE,"E102");Q64=makeQuery(id+"F0.imprint","IMPRINT",FACE,{"disambiguationData":[TD([[makeQuery(id+"F0.imprint","IMPRINT",EDGE,{"derivedFrom":subQ5}),1.0]])]});}
            var Q65;
            {var subQ5=sQuery(id+"F0.wireOp",EDGE,"E104");Q65=makeQuery(id+"F0.imprint","IMPRINT",FACE,{"disambiguationData":[TD([[makeQuery(id+"F0.imprint","IMPRINT",EDGE,{"derivedFrom":subQ5}),1.0]])]});}
            extrude(context, id + "F2", {"entities" : qUnion([Q0, Q1, Q2, Q3, Q4, Q5, Q6, Q7, Q8, Q9, Q10, Q11, Q12, Q13, Q14, Q15, Q16, Q17, Q18, Q19, Q20, Q21, Q22, Q23, Q24, Q25, Q26, Q27, Q28, Q29, Q30, Q31, Q32, Q33, Q34, Q35, Q36, Q37, Q38, Q39, Q40, Q41, Q42, Q43, Q44, Q45, Q46, Q47, Q48, Q49, Q50, Q51, Q52, Q53, Q54, Q55, Q56, Q57, Q58, Q59, Q60, Q61, Q62, Q63, Q64, Q65]), "operationType" : NewBodyOperationType.ADD, "depth" : 1 * mm, "offsetDistance" : 25 * mm});
        }
    });
